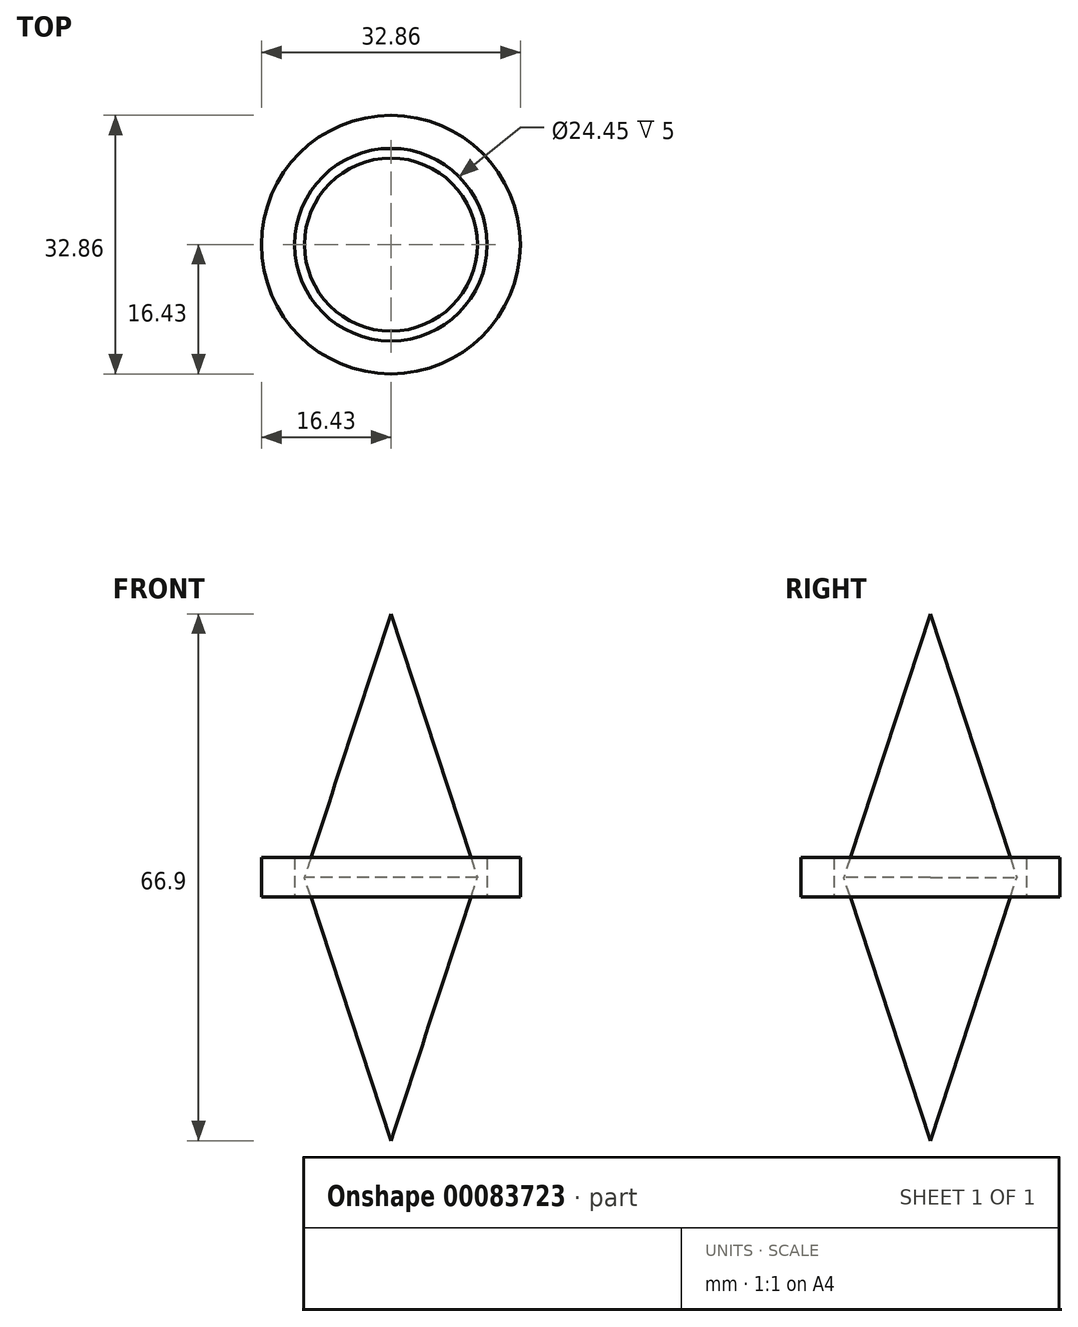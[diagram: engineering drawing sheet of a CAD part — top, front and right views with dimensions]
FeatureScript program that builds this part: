
annotation { "Feature Type Name" : "Feature", "Feature Type Description" : "" }
export const myFeature = defineFeature(function(context is Context, id is Id, definition is map)
    precondition{}
    {
        {
            var Q0;
            Q0=qCreatedBy(makeId("Top.planeOp"),FACE);
            var sketch = newSketch(context, id + "F0", { "sketchPlane" : qUnion([Q0])});
            skCircle(sketch, "E0", {"center": v(0, 0) * mm, "radius": 16.43 * mm});
            skCircle(sketch, "E1", {"center": v(0, 0) * mm, "radius": 12.22 * mm});
            skSolve(sketch);
        }
        {
            var Q0;
            Q0 = qSketchRegion(id + "F0", true);
            extrude(context, id + "F1", {"entities" : qUnion([Q0]), "endBound" : BoundingType.SYMMETRIC, "depth" : 5 * mm});
        }
        {
            var Q0;
            Q0=qCreatedBy(makeId("Front.planeOp"),FACE);
            var sketch = newSketch(context, id + "F2", { "sketchPlane" : qUnion([Q0])});
            skLineSegment(sketch, "E2", {"start": v(0, 33.45) * mm, "end": v(-10.99, 0) * mm});
            skLineSegment(sketch, "E3", {"start": v(-10.99, 0) * mm, "end": v(0, -33.45) * mm});
            skLineSegment(sketch, "E4", {"start": v(0, 33.45) * mm, "end": v(0, -33.45) * mm});
            skSolve(sketch);
        }
        {
            var Q0;
            Q0 = qSketchRegion(id + "F2", true);
            var Q1;
            Q1=sQuery(id+"F2.wireOp",EDGE,"E4");
            revolve(context, id + "F3", {"entities" : qUnion([Q0]), "axis" : qUnion([Q1]), "revolveType" : RevolveType.FULL});
        }
    });
